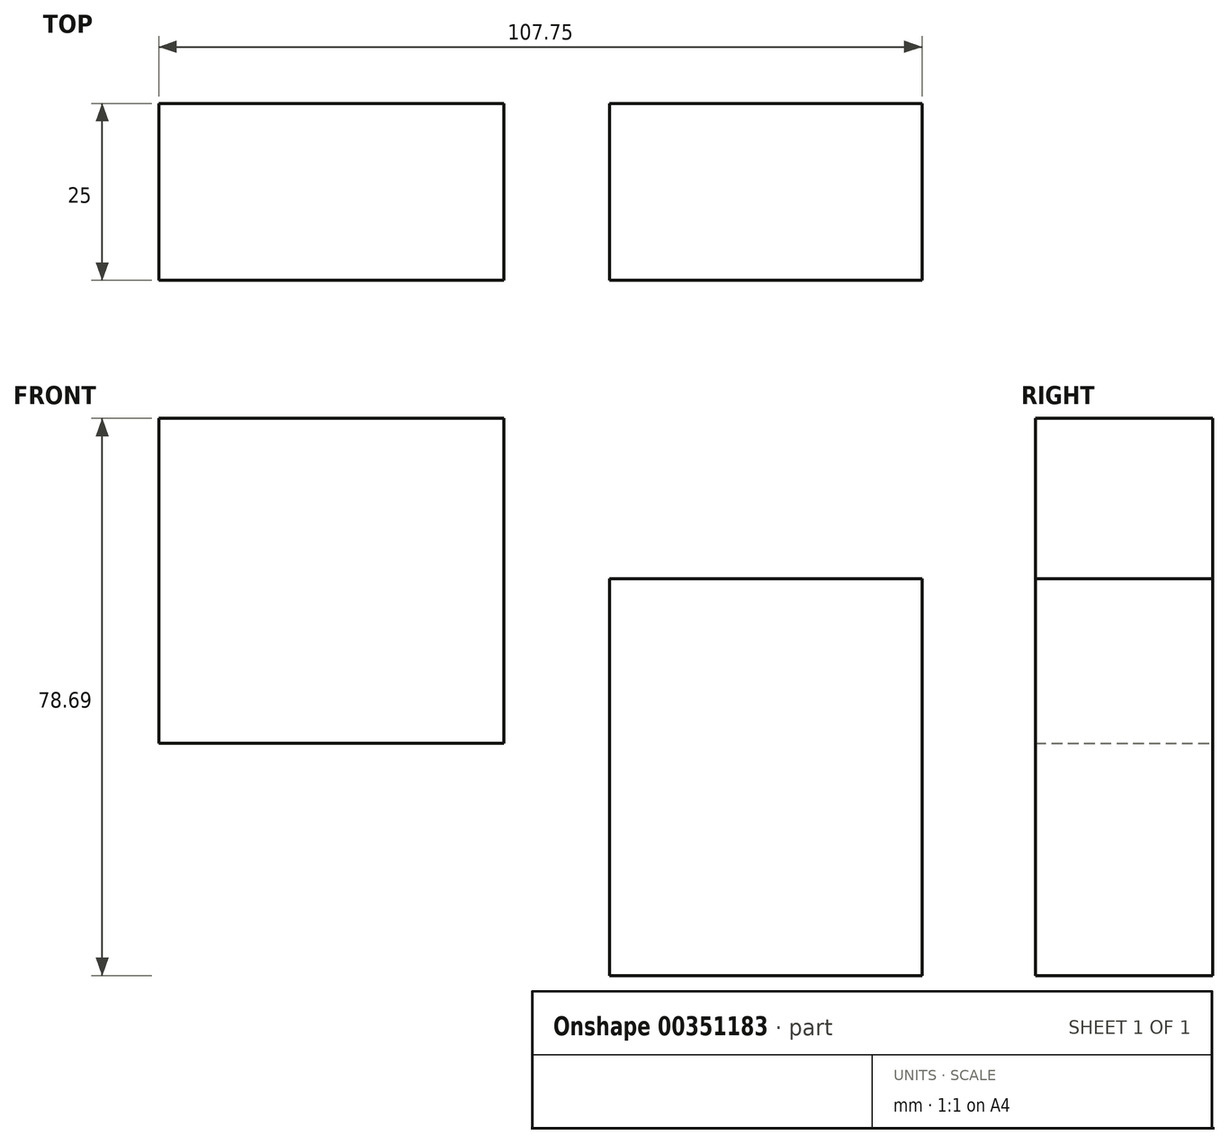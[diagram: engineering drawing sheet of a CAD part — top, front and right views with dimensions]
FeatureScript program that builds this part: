
annotation { "Feature Type Name" : "Feature", "Feature Type Description" : "" }
export const myFeature = defineFeature(function(context is Context, id is Id, definition is map)
    precondition{}
    {
        {
            var Q0;
            Q0=qCreatedBy(makeId("Front.planeOp"),FACE);
            var sketch = newSketch(context, id + "F0", { "sketchPlane" : qUnion([Q0])});
            skLineSegment(sketch, "E0.bottom", {"start": v(-107.75, 32.83) * mm, "end": v(-59.07, 32.83) * mm});
            skLineSegment(sketch, "E0.top", {"start": v(-107.75, 78.7) * mm, "end": v(-59.07, 78.7) * mm});
            skLineSegment(sketch, "E0.left", {"start": v(-107.75, 32.83) * mm, "end": v(-107.75, 78.7) * mm});
            skLineSegment(sketch, "E0.right", {"start": v(-59.07, 32.83) * mm, "end": v(-59.07, 78.7) * mm});
            skPoint(sketch, "E0.middle", {"position": v(-83.41, 55.76) * mm});
            skLineSegment(sketch, "E1.bottom", {"start": v(-44.14, 0) * mm, "end": v(0, 0) * mm});
            skLineSegment(sketch, "E1.top", {"start": v(-44.14, 56.06) * mm, "end": v(0, 56.06) * mm});
            skLineSegment(sketch, "E1.left", {"start": v(-44.14, 0) * mm, "end": v(-44.14, 56.06) * mm});
            skLineSegment(sketch, "E1.right", {"start": v(0, 0) * mm, "end": v(0, 56.06) * mm});
            skPoint(sketch, "E1.middle", {"position": v(-22.07, 28.03) * mm});
            skSolve(sketch);
        }
        {
            var Q0;
            Q0=makeQuery(id+"F0.imprint","IMPRINT",FACE,{"disambiguationData":[TD([[makeQuery(id+"F0.imprint","IMPRINT",EDGE,{"derivedFrom":sQuery(id+"F0.wireOp",EDGE,"E0.bottom")}),1.0]])]});
            var Q1;
            Q1=makeQuery(id+"F0.imprint","IMPRINT",FACE,{"disambiguationData":[TD([[makeQuery(id+"F0.imprint","IMPRINT",EDGE,{"derivedFrom":sQuery(id+"F0.wireOp",EDGE,"E1.bottom")}),1.0]])]});
            extrude(context, id + "F1", {"entities" : qUnion([Q0, Q1]), "depth" : 25 * mm});
        }
    });
